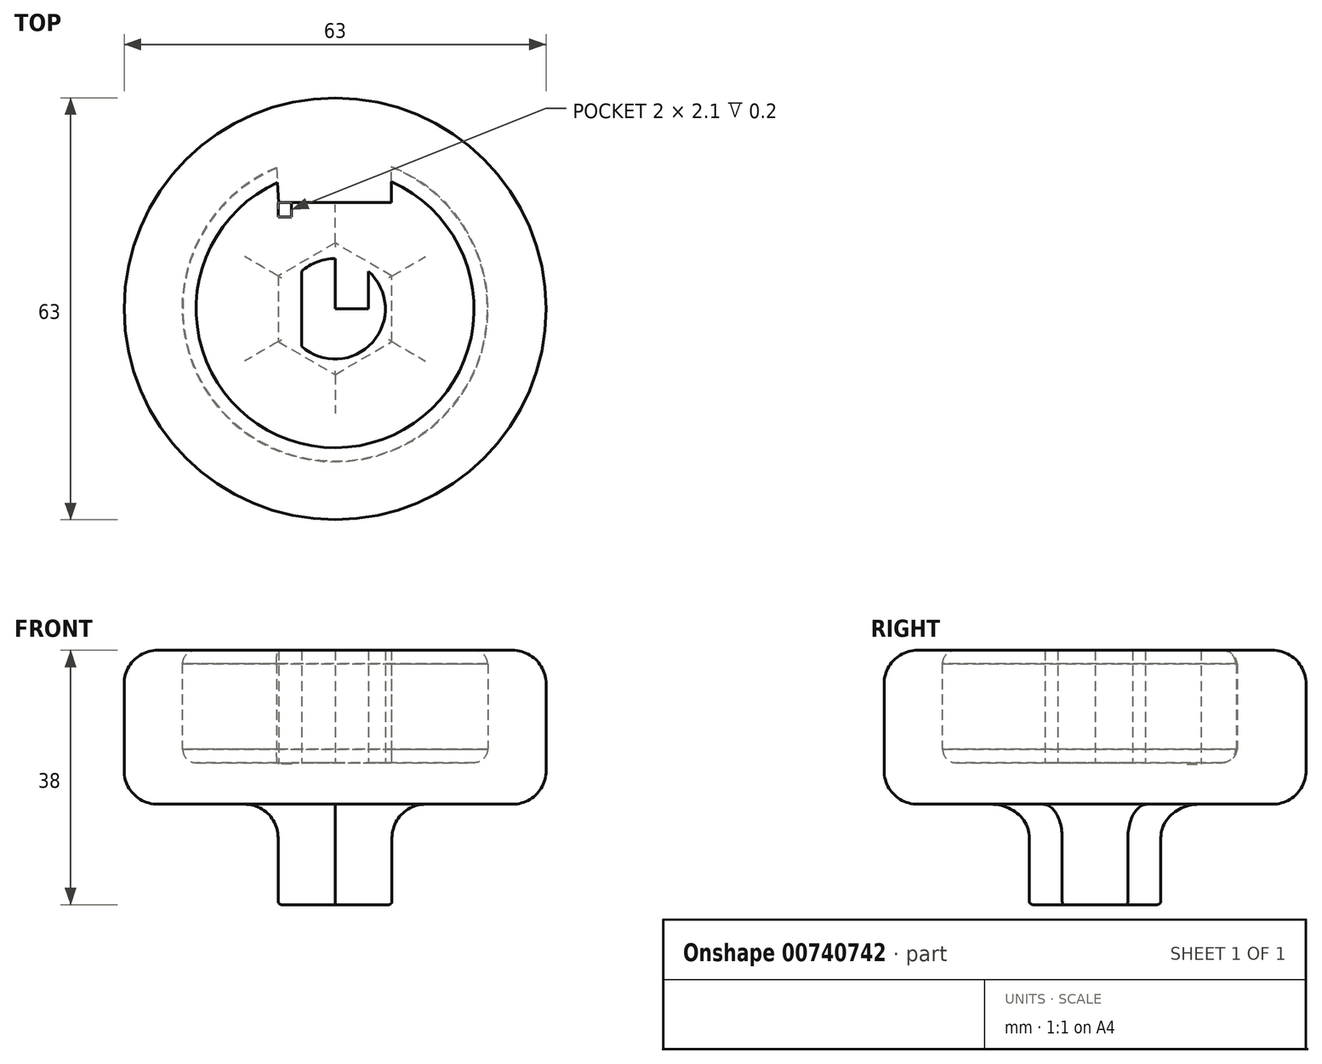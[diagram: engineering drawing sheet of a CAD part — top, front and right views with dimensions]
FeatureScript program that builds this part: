
annotation { "Feature Type Name" : "Feature", "Feature Type Description" : "" }
export const myFeature = defineFeature(function(context is Context, id is Id, definition is map)
    precondition{}
    {
        {
            var Q0;
            Q0=qCreatedBy(makeId("Top.planeOp"),FACE);
            var sketch = newSketch(context, id + "F0", { "sketchPlane" : qUnion([Q0])});
            skCircle(sketch, "E0", {"center": v(0, 0) * mm, "radius": 22.75 * mm});
            skCircle(sketch, "E1", {"center": v(0, 0) * mm, "radius": 7.5 * mm});
            skLineSegment(sketch, "E2", {"start": v(0, 0) * mm, "end": v(5, 0) * mm});
            skLineSegment(sketch, "E3", {"start": v(5, 0) * mm, "end": v(5, -5.6) * mm});
            skLineSegment(sketch, "E4", {"start": v(5, -5.6) * mm, "end": v(5, 5.6) * mm});
            skLineSegment(sketch, "E5", {"start": v(0, 0) * mm, "end": v(-5, 0) * mm});
            skLineSegment(sketch, "E6", {"start": v(-5, 5.6) * mm, "end": v(-5, -5.6) * mm});
            skLineSegment(sketch, "E7", {"start": v(0, 0) * mm, "end": v(0, 22.75) * mm});
            skLineSegment(sketch, "E8", {"start": v(0, 22.75) * mm, "end": v(0, 15.75) * mm});
            skLineSegment(sketch, "E9", {"start": v(8.5, 15.75) * mm, "end": v(0, 15.75) * mm});
            skLineSegment(sketch, "E10", {"start": v(8.5, 15.75) * mm, "end": v(8.5, 21.1) * mm});
            skLineSegment(sketch, "E11", {"start": v(0, 15.75) * mm, "end": v(-8.5, 15.75) * mm});
            skLineSegment(sketch, "E12", {"start": v(-8.5, 15.75) * mm, "end": v(-8.83, 21.1) * mm});
            skLineSegment(sketch, "E13", {"start": v(-8.5, 15.75) * mm, "end": v(-8.5, 13.75) * mm});
            skLineSegment(sketch, "E14", {"start": v(-8.5, 13.75) * mm, "end": v(-6.5, 13.75) * mm});
            skLineSegment(sketch, "E15", {"start": v(-6.5, 13.75) * mm, "end": v(-6.5, 15.75) * mm});
            skSolve(sketch);
        }
        {
            var Q0;
            Q0=makeQuery(id+"F0.imprint","IMPRINT",FACE,{"disambiguationData":[TD([[makeQuery(id+"F0.imprint","IMPRINT",EDGE,{"derivedFrom":sQuery(id+"F0.wireOp",EDGE,"E9")}),1.0]])]});
            var Q1;
            {var subQ0=sQuery(id+"F0.wireOp",EDGE,"E4");var subQ1=sQuery(id+"F0.wireOp",EDGE,"E1");var subQ2=makeQuery(id+"F0.imprint","INTERSECT",VERTEX,{"disambiguationData":[OD(0.0)],"derivedFrom":[subQ1,subQ0]});Q1=makeQuery(id+"F0.imprint","IMPRINT",FACE,{"disambiguationData":[TD([[makeQuery(id+"F0.imprint","IMPRINT",EDGE,{"disambiguationData":[TD([[subQ2,-1.0]])],"derivedFrom":subQ1}),1.0]])]});}
            var Q2;
            {var subQ0=sQuery(id+"F0.wireOp",EDGE,"E6");var subQ1=sQuery(id+"F0.wireOp",EDGE,"E1");var subQ2=makeQuery(id+"F0.imprint","INTERSECT",VERTEX,{"disambiguationData":[OD(0.0)],"derivedFrom":[subQ1,subQ0]});Q2=makeQuery(id+"F0.imprint","IMPRINT",FACE,{"disambiguationData":[TD([[makeQuery(id+"F0.imprint","IMPRINT",EDGE,{"disambiguationData":[TD([[subQ2,-1.0]])],"derivedFrom":subQ1}),1.0]])]});}
            extrude(context, id + "F1", {"entities" : qUnion([Q0, Q1, Q2]), "depth" : 16.8 * mm, "offsetDistance" : 25 * mm});
        }
        {
            var Q0;
            Q0=makeQuery(id+"F1.opExtrude","CAP_EDGE",EDGE,{"disambiguationData":[OSD([sQuery(id+"F0.wireOp",EDGE,"E0")])],"isStart":false});
            var Q1;
            Q1=makeQuery(id+"F1.opExtrude","CAP_EDGE",EDGE,{"disambiguationData":[OSD([sQuery(id+"F0.wireOp",EDGE,"E0")])],"isStart":true});
            fillet(context, id + "F2", {"entities" : qUnion([Q0, Q1]), "radius" : 2 * mm, "tangentPropagation" : true, "allowEdgeOverflow" : false});
        }
        {
            var Q0;
            Q0=makeQuery(id+"F1.opExtrude","CAP_FACE",FACE,{"disambiguationData":[OSD([sQuery(id+"F0.wireOp",EDGE,"E0"),sQuery(id+"F0.wireOp",EDGE,"E1"),sQuery(id+"F0.wireOp",EDGE,"E4"),sQuery(id+"F0.wireOp",EDGE,"E6"),sQuery(id+"F0.wireOp",EDGE,"E9"),sQuery(id+"F0.wireOp",EDGE,"E10"),sQuery(id+"F0.wireOp",EDGE,"E11"),sQuery(id+"F0.wireOp",EDGE,"E12")])],"isStart":false});
            var sketch = newSketch(context, id + "F3", { "sketchPlane" : qUnion([Q0])});
            skLineSegment(sketch, "E16", {"start": v(-8.5, 15.75) * mm, "end": v(-8.5, 13.75) * mm});
            skLineSegment(sketch, "E17", {"start": v(-8.5, 13.75) * mm, "end": v(-6.5, 13.75) * mm});
            skLineSegment(sketch, "E18", {"start": v(-6.5, 13.75) * mm, "end": v(-6.5, 15.75) * mm});
            skSolve(sketch);
        }
        {
            var Q0;
            {var subQ0=sQuery(id+"F0.wireOp",EDGE,"E13");Q0=makeQuery(id+"F0.imprint","IMPRINT",FACE,{"disambiguationData":[TD([[makeQuery(id+"F0.imprint","IMPRINT",EDGE,{"derivedFrom":subQ0}),1.0]])]});}
            extrude(context, id + "F4", {"entities" : qUnion([Q0]), "operationType" : NewBodyOperationType.ADD, "depth" : 17.1 * mm, "offsetDistance" : 25 * mm, "hasSecondDirection" : true, "secondDirectionOppositeDirection" : true, "secondDirectionDepth" : .2 * mm});
        }
        {
            var Q0;
            Q0=makeQuery(id+"F3.imprint","IMPRINT",FACE,{"disambiguationData":[TD([[makeQuery(id+"F3.imprint","IMPRINT",EDGE,{"derivedFrom":sQuery(id+"F3.wireOp",EDGE,"E16")}),-1.0]])]});
            var sketch = newSketch(context, id + "F5", { "sketchPlane" : qUnion([Q0])});
            skCircle(sketch, "E19", {"center": v(0, 0) * mm, "radius": 31.5 * mm});
            skSolve(sketch);
        }
        {
            var Q0;
            Q0 = qSketchRegion(id + "F5", true);
            extrude(context, id + "F6", {"entities" : qUnion([Q0]), "oppositeDirection" : true, "depth" : 23 * mm, "offsetDistance" : 25 * mm});
        }
        {
            var Q0;
            Q0=makeQuery(id+"F6.opExtrude","CAP_FACE",FACE,{"disambiguationData":[OSD([sQuery(id+"F5.wireOp",EDGE,"E19")])],"isStart":false});
            var sketch = newSketch(context, id + "F7", { "sketchPlane" : qUnion([Q0])});
            skLineSegment(sketch, "E20", {"start": v(0, 0) * mm, "end": v(-8.5, 0) * mm});
            skCircle(sketch, "E21.cCircle", {"center": v(0, 0) * mm, "radius": 8.5 * mm, "construction": true});
            skLineSegment(sketch, "E21.0", {"start": v(-8.5, -4.9) * mm, "end": v(-8.5, 4.9) * mm});
            skLineSegment(sketch, "E21.1", {"start": v(-8.5, 4.9) * mm, "end": v(0, 9.81) * mm});
            skLineSegment(sketch, "E21.2", {"start": v(0, 9.81) * mm, "end": v(8.5, 4.9) * mm});
            skLineSegment(sketch, "E21.3", {"start": v(8.5, 4.9) * mm, "end": v(8.5, -4.9) * mm});
            skLineSegment(sketch, "E21.4", {"start": v(8.5, -4.9) * mm, "end": v(0, -9.81) * mm});
            skLineSegment(sketch, "E21.5", {"start": v(0, -9.81) * mm, "end": v(-8.5, -4.9) * mm});
            skPoint(sketch, "E21.0.midPoint", {"position": v(-8.5, 0) * mm});
            skSolve(sketch);
        }
        {
            var Q0;
            Q0=makeQuery(id+"F1.opExtrude","SWEPT_BODY",BODY,{"disambiguationData":[OSD([sQuery(id+"F0.wireOp",EDGE,"E0"),sQuery(id+"F0.wireOp",EDGE,"E1"),sQuery(id+"F0.wireOp",EDGE,"E4"),sQuery(id+"F0.wireOp",EDGE,"E6"),sQuery(id+"F0.wireOp",EDGE,"E9"),sQuery(id+"F0.wireOp",EDGE,"E10"),sQuery(id+"F0.wireOp",EDGE,"E11"),sQuery(id+"F0.wireOp",EDGE,"E12"),sQuery(id+"F0.wireOp",EDGE,"E13"),sQuery(id+"F0.wireOp",EDGE,"E14"),sQuery(id+"F0.wireOp",EDGE,"E15")])]});
            var Q1;
            Q1=makeQuery(id+"F6.opExtrude","SWEPT_BODY",BODY,{"disambiguationData":[OSD([sQuery(id+"F5.wireOp",EDGE,"E19")])]});
            var Q2;
            Q2=makeQuery(id+"F1.opExtrude","SWEPT_FACE",FACE,{"disambiguationData":[OSD([sQuery(id+"F0.wireOp",EDGE,"E0")])]});
            var Q3;
            Q3=makeQuery(id+"F1.opExtrude","SWEPT_FACE",FACE,{"disambiguationData":[OSD([sQuery(id+"F0.wireOp",EDGE,"E12")])]});
            var Q4;
            {var subQ0=sQuery(id+"F0.wireOp",EDGE,"E11");Q4=makeQuery(id+"F4.boolean.opBoolean","MERGE",FACE,{"derivedFrom":[makeQuery(id+"F1.opExtrude","SWEPT_FACE",FACE,{"disambiguationData":[OSD([sQuery(id+"F0.wireOp",EDGE,"E9"),subQ0])]}),makeQuery(id+"F4.opExtrude","SWEPT_FACE",FACE,{"disambiguationData":[OSD([subQ0])]})]});}
            var Q5;
            Q5=makeQuery(id+"F1.opExtrude","SWEPT_FACE",FACE,{"disambiguationData":[OSD([sQuery(id+"F0.wireOp",EDGE,"E10")])]});
            booleanBodies(context, id + "F8", {"operationType" : BooleanOperationType.SUBTRACTION, "tools" : qUnion([Q0]), "targets" : qUnion([Q1]), "offset" : true, "entitiesToOffset" : qUnion([Q2, Q3, Q4, Q5]), "offsetDistance" : .1 * mm});
        }
        {
            var Q0;
            {var subQ0=sQuery(id+"F7.wireOp",EDGE,"E21.1");Q0=makeQuery(id+"F7.imprint","IMPRINT",FACE,{"disambiguationData":[TD([[makeQuery(id+"F7.imprint","IMPRINT",EDGE,{"derivedFrom":subQ0}),-1.0]])]});}
            extrude(context, id + "F9", {"entities" : qUnion([Q0]), "operationType" : NewBodyOperationType.ADD, "depth" : 15 * mm, "offsetDistance" : 25 * mm});
        }
        {
            var Q0;
            Q0=makeQuery(id+"F6.opExtrude","CAP_FACE",FACE,{"disambiguationData":[OSD([sQuery(id+"F5.wireOp",EDGE,"E19")])],"isStart":false});
            var Q1;
            Q1=makeQuery(id+"F6.opExtrude","CAP_EDGE",EDGE,{"disambiguationData":[OSD([sQuery(id+"F5.wireOp",EDGE,"E19")])],"isStart":true});
            fillet(context, id + "F10", {"entities" : qUnion([Q0, Q1]), "radius" : 5 * mm, "tangentPropagation" : true, "allowEdgeOverflow" : false});
        }
        {
            var Q0;
            Q0=makeQuery(id+"F9.opExtrude","CAP_FACE",FACE,{"disambiguationData":[OSD([sQuery(id+"F7.wireOp",EDGE,"E21.0"),sQuery(id+"F7.wireOp",EDGE,"E21.1"),sQuery(id+"F7.wireOp",EDGE,"E21.2"),sQuery(id+"F7.wireOp",EDGE,"E21.3"),sQuery(id+"F7.wireOp",EDGE,"E21.4"),sQuery(id+"F7.wireOp",EDGE,"E21.5")])],"isStart":false});
            fillet(context, id + "F11", {"entities" : qUnion([Q0]), "radius" : .5 * mm, "tangentPropagation" : true, "allowEdgeOverflow" : false});
        }
        {
            var Q0;
            {var subQ3=sQuery(id+"F0.wireOp",EDGE,"E4");Q0=makeQuery(id+"F3.imprint","IMPRINT",FACE,{"disambiguationData":[TD([[makeQuery(id+"F3.imprint","IMPRINT",EDGE,{"derivedFrom":makeQuery(id+"F1.opExtrude","CAP_EDGE",EDGE,{"disambiguationData":[OSD([subQ3])],"isStart":false})}),1.0]])]});}
            extrude(context, id + "F12", {"entities" : qUnion([Q0]), "operationType" : NewBodyOperationType.REMOVE, "oppositeDirection" : true, "depth" : 16 * mm, "offsetDistance" : 25 * mm});
        }
    });
